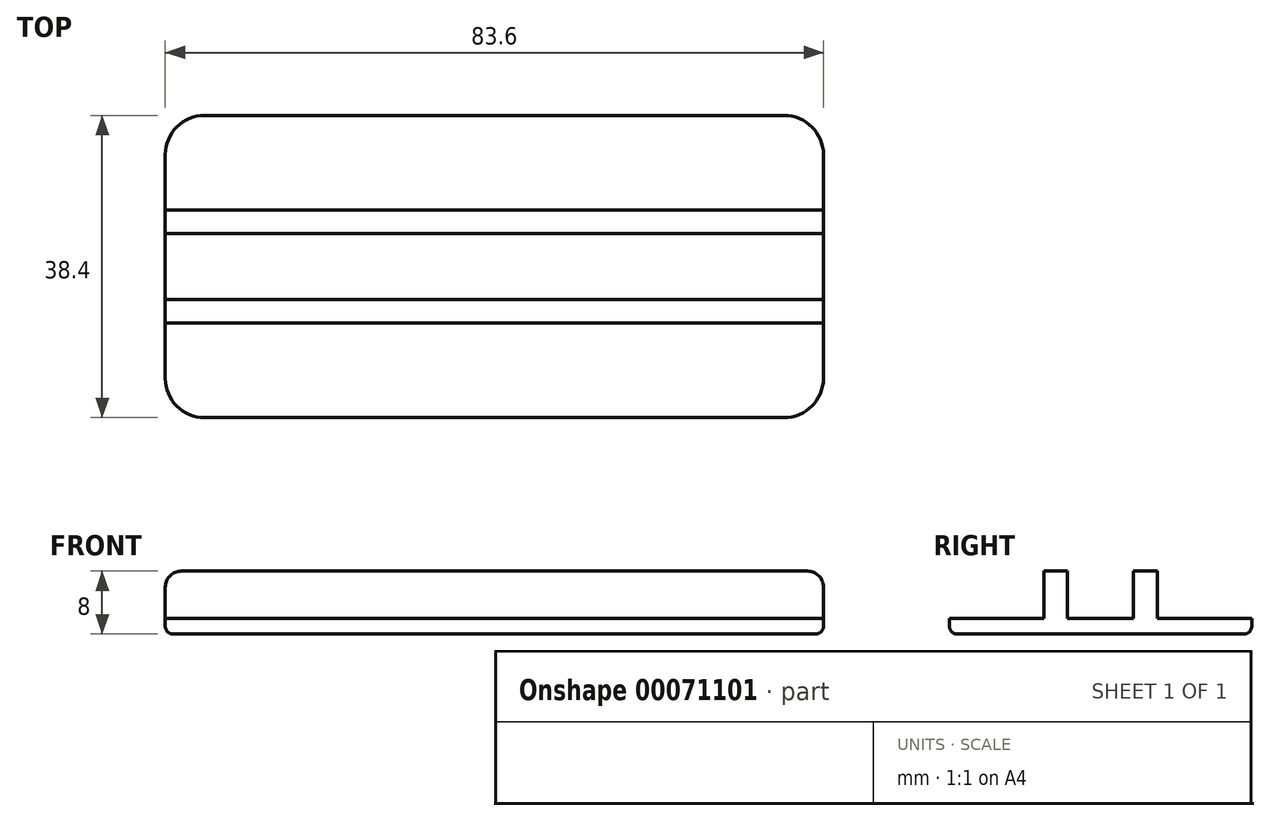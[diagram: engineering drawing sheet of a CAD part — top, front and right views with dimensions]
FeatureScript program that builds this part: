
annotation { "Feature Type Name" : "Feature", "Feature Type Description" : "" }
export const myFeature = defineFeature(function(context is Context, id is Id, definition is map)
    precondition{}
    {
        {
            var Q0;
            Q0=qCreatedBy(makeId("Top.planeOp"),FACE);
            var sketch = newSketch(context, id + "F0", { "sketchPlane" : qUnion([Q0])});
            skLineSegment(sketch, "E0.bottom", {"start": v(0, 0) * mm, "end": v(83.6, 0) * mm});
            skLineSegment(sketch, "E0.top", {"start": v(0, 8.4) * mm, "end": v(83.6, 8.4) * mm});
            skLineSegment(sketch, "E0.left", {"start": v(0, 0) * mm, "end": v(0, 8.4) * mm});
            skLineSegment(sketch, "E0.right", {"start": v(83.6, 0) * mm, "end": v(83.6, 8.4) * mm});
            skLineSegment(sketch, "E1.top", {"start": v(0, 23.4) * mm, "end": v(83.6, 23.4) * mm});
            skLineSegment(sketch, "E1.left", {"start": v(0, 8.4) * mm, "end": v(0, 23.4) * mm});
            skLineSegment(sketch, "E1.right", {"start": v(83.6, 8.4) * mm, "end": v(83.6, 23.4) * mm});
            skLineSegment(sketch, "E2", {"start": v(0, 4.2) * mm, "end": v(83.6, 4.2) * mm, "construction": true});
            skLineSegment(sketch, "E3.MirrorCS", {"start": v(0, -15) * mm, "end": v(83.6, -15) * mm});
            skLineSegment(sketch, "E4.MirrorCS", {"start": v(0, 0) * mm, "end": v(0, -15) * mm});
            skLineSegment(sketch, "E5.MirrorCS", {"start": v(83.6, 0) * mm, "end": v(83.6, -15) * mm});
            skLineSegment(sketch, "E6", {"start": v(0, 11.4) * mm, "end": v(83.6, 11.4) * mm});
            skLineSegment(sketch, "E7.MirrorCS", {"start": v(0, -3) * mm, "end": v(83.6, -3) * mm});
            skSolve(sketch);
        }
        {
            var Q0;
            Q0=makeQuery(id+"F0.imprint","IMPRINT",FACE,{"disambiguationData":[TD([[makeQuery(id+"F0.imprint","IMPRINT",EDGE,{"derivedFrom":sQuery(id+"F0.wireOp",EDGE,"E0.top")}),1.0]])]});
            var Q1;
            Q1=makeQuery(id+"F0.imprint","IMPRINT",FACE,{"disambiguationData":[TD([[makeQuery(id+"F0.imprint","IMPRINT",EDGE,{"derivedFrom":sQuery(id+"F0.wireOp",EDGE,"E0.bottom")}),-1.0]])]});
            var Q2;
            Q2=makeQuery(id+"F0.imprint","IMPRINT",FACE,{"disambiguationData":[TD([[makeQuery(id+"F0.imprint","IMPRINT",EDGE,{"derivedFrom":sQuery(id+"F0.wireOp",EDGE,"E0.bottom")}),1.0]])]});
            var Q3;
            {var subQ0=sQuery(id+"F0.wireOp",EDGE,"E1.top");Q3=makeQuery(id+"F0.imprint","IMPRINT",FACE,{"disambiguationData":[TD([[makeQuery(id+"F0.imprint","IMPRINT",EDGE,{"derivedFrom":subQ0}),-1.0]])]});}
            var Q4;
            {var subQ0=sQuery(id+"F0.wireOp",EDGE,"E3.MirrorCS");Q4=makeQuery(id+"F0.imprint","IMPRINT",FACE,{"disambiguationData":[TD([[makeQuery(id+"F0.imprint","IMPRINT",EDGE,{"derivedFrom":subQ0}),1.0]])]});}
            extrude(context, id + "F1", {"entities" : qUnion([Q0, Q1, Q2, Q3, Q4]), "oppositeDirection" : true, "depth" : 2 * mm});
        }
        {
            var Q0;
            {var subQ0=sQuery(id+"F0.wireOp",EDGE,"E0.top");Q0=makeQuery(id+"F0.imprint","IMPRINT",FACE,{"disambiguationData":[TD([[makeQuery(id+"F0.imprint","IMPRINT",EDGE,{"derivedFrom":subQ0}),1.0]])]});}
            var Q1;
            {var subQ0=sQuery(id+"F0.wireOp",EDGE,"E0.bottom");Q1=makeQuery(id+"F0.imprint","IMPRINT",FACE,{"disambiguationData":[TD([[makeQuery(id+"F0.imprint","IMPRINT",EDGE,{"derivedFrom":subQ0}),-1.0]])]});}
            extrude(context, id + "F2", {"entities" : qUnion([Q0, Q1]), "operationType" : NewBodyOperationType.ADD, "depth" : 6 * mm});
        }
        {
            var Q0;
            Q0=makeQuery(id+"F2.opExtrude","CAP_EDGE",EDGE,{"disambiguationData":[OSD([sQuery(id+"F0.wireOp",EDGE,"E1.left")])],"isStart":false});
            var Q1;
            Q1=makeQuery(id+"F2.opExtrude","CAP_EDGE",EDGE,{"disambiguationData":[OSD([sQuery(id+"F0.wireOp",EDGE,"E4.MirrorCS")])],"isStart":false});
            var Q2;
            Q2=makeQuery(id+"F2.opExtrude","CAP_EDGE",EDGE,{"disambiguationData":[OSD([sQuery(id+"F0.wireOp",EDGE,"E1.right")])],"isStart":false});
            var Q3;
            Q3=makeQuery(id+"F2.opExtrude","CAP_EDGE",EDGE,{"disambiguationData":[OSD([sQuery(id+"F0.wireOp",EDGE,"E5.MirrorCS")])],"isStart":false});
            fillet(context, id + "F3", {"entities" : qUnion([Q0, Q1, Q2, Q3]), "radius" : 2 * mm, "tangentPropagation" : true, "allowEdgeOverflow" : false});
        }
        {
            var Q0;
            Q0=makeQuery(id+"F1.opExtrude","SWEPT_EDGE",EDGE,{"disambiguationData":[OSD([sQuery(id+"F0.wireOp",EDGE,"E3.MirrorCS"),sQuery(id+"F0.wireOp",EDGE,"E5.MirrorCS")])]});
            var Q1;
            Q1=makeQuery(id+"F1.opExtrude","SWEPT_EDGE",EDGE,{"disambiguationData":[OSD([sQuery(id+"F0.wireOp",EDGE,"E1.top"),sQuery(id+"F0.wireOp",EDGE,"E1.right")])]});
            var Q2;
            Q2=makeQuery(id+"F1.opExtrude","SWEPT_EDGE",EDGE,{"disambiguationData":[OSD([sQuery(id+"F0.wireOp",EDGE,"E1.top"),sQuery(id+"F0.wireOp",EDGE,"E1.left")])]});
            var Q3;
            Q3=makeQuery(id+"F1.opExtrude","SWEPT_EDGE",EDGE,{"disambiguationData":[OSD([sQuery(id+"F0.wireOp",EDGE,"E3.MirrorCS"),sQuery(id+"F0.wireOp",EDGE,"E4.MirrorCS")])]});
            fillet(context, id + "F4", {"entities" : qUnion([Q0, Q1, Q2, Q3]), "radius" : 5 * mm, "tangentPropagation" : true, "allowEdgeOverflow" : false});
        }
        {
            var Q0;
            Q0=makeQuery(id+"F1.opExtrude","CAP_EDGE",EDGE,{"disambiguationData":[OSD([sQuery(id+"F0.wireOp",EDGE,"E1.top")])],"isStart":false});
            fillet(context, id + "F5", {"entities" : qUnion([Q0]), "radius" : 1 * mm, "tangentPropagation" : true, "allowEdgeOverflow" : false});
        }
    });
